# Revit family: Indoor_Floor Lamp_Santa&Cole_Pie de Salón
name_source: partatom
category: Luminarias
revit_build: Autodesk Revit 2018 (Build: 20190510_1515(x64)
units: mm (PartAtom-declared; Revit-internal decimal feet)

## family parameters
Compartido = No
Corte con vacíos al cargar = No
Cota de conector redondo = Diámetro de uso
Número OmniClass = 23.80.70.00
Origen de luz = Sí
Punto de cálculo de habitación = No
Se basa en plano de trabajo = No
Siempre vertical = Sí
Tipo de pieza = Normal
Título OmniClass = Lighting

## types (19) — shared parameters
Assembly instructions - CE = https://www.santacole.com
Assembly instructions - UL = https://www.santacole.com
Cambio de temperatura de color de luz atenuada = <Ninguno>
Carga aparente = 12 VA
Energy Label = https://www.santacole.com
Fabricante = Santa & Cole
Filtro de color = 16777215
Load = 12 W
Manufacturer website = http://www.santacole.com
Modelo = Pie de Salón
Tamaño de símbolo de origen de luz = 50 mm  [stored 0.164042 ft]
Technical Information = https://www.santacole.com
URL = https://www.santacole.com

## per-type parameters (varying)
| type | Code | Lampshade Material | Visibility_G1 | Visibility_G2 | Visibility_G3 |
| G1 - Beige Cardboard Lampshade | PDS0x+PG10x | Santa & Cole - Beige Cardboard | Sí | No | No |
| G1 - Natural Ribbon Lampshade | PDS0x+PG10x | Santa & Cole - Natural Ribbon | Sí | No | No |
| G1 - Red-amber Ribbon Lampshade | PDS0x+PG10x | Santa & Cole - Red-amber Ribbon | Sí | No | No |
| G1 - Black Ribbon Lampshade | PDS0x+PG10x | Santa & Cole - Black Ribbon | Sí | No | No |
| G1 - Terracota Raw Color Ribbon Lampshade | PDS0x+PG10x | Santa & Cole - Terracota Raw Color Ribbon | Sí | No | No |
| G1 - Mustard Raw Color Ribbon Lampshade | PDS0x+PG10x | Santa & Cole - Mustard Raw Color Ribbon | Sí | No | No |
| G1 - Green Raw Color Ribbon Lampshade | PDS0x+PG10x | Santa & Cole - Green Raw Color Ribbon | Sí | No | No |
| G1 - White Linen Lampshade | PDS0x+PG10x | Santa & Cole - White Linen | Sí | No | No |
| G2 - Natural Ribbon Lampshade | PDS0x+PG20x | Santa & Cole - Natural Ribbon | No | Sí | No |
| G2 - Red-amber Ribbon Lampshade | PDS0x+PG20x | Santa & Cole - Red-amber Ribbon | No | Sí | No |
| G2 - Black Ribbon Lampshade | PDS0x+PG20x | Santa & Cole - Black Ribbon | No | Sí | No |
| G2 - White Linen Lampshade | PDS0x+PG20x | Santa & Cole - White Linen | No | Sí | No |
| G3 - Natural Ribbon Lampshade | PDS0x+PG30x | Santa & Cole - Natural Ribbon | No | No | Sí |
| G3 - Red-amber Ribbon Lampshade | PDS0x+PG30x | Santa & Cole - Red-amber Ribbon | No | No | Sí |
| G3 - Black Ribbon Lampshade | PDS0x+PG30x | Santa & Cole - Black Ribbon | No | No | Sí |
| G3 - Terracota Raw Color Ribbon Lampshade | PDS0x+PG30x | Santa & Cole - Terracota Raw Color Ribbon | No | No | Sí |
| G3 - Mustard Raw Color Ribbon Lampshade | PDS0x+PG30x | Santa & Cole - Mustard Raw Color Ribbon | No | No | Sí |
| G3 - Green Raw Color Ribbon Lampshade | PDS0x+PG30x | Santa & Cole - Green Raw Color Ribbon | No | No | Sí |
| G3 - White Linen Lampshade | PDS0x+PG30x | Santa & Cole - White Linen | No | No | Sí |

note: [stored X ft] marks values corroborated as IEEE doubles in the binary element streams (Revit-internal decimal feet)

## geometry (parser evidence)
native form markers: Sweep x1
no freeform markers — native parametric forms only
